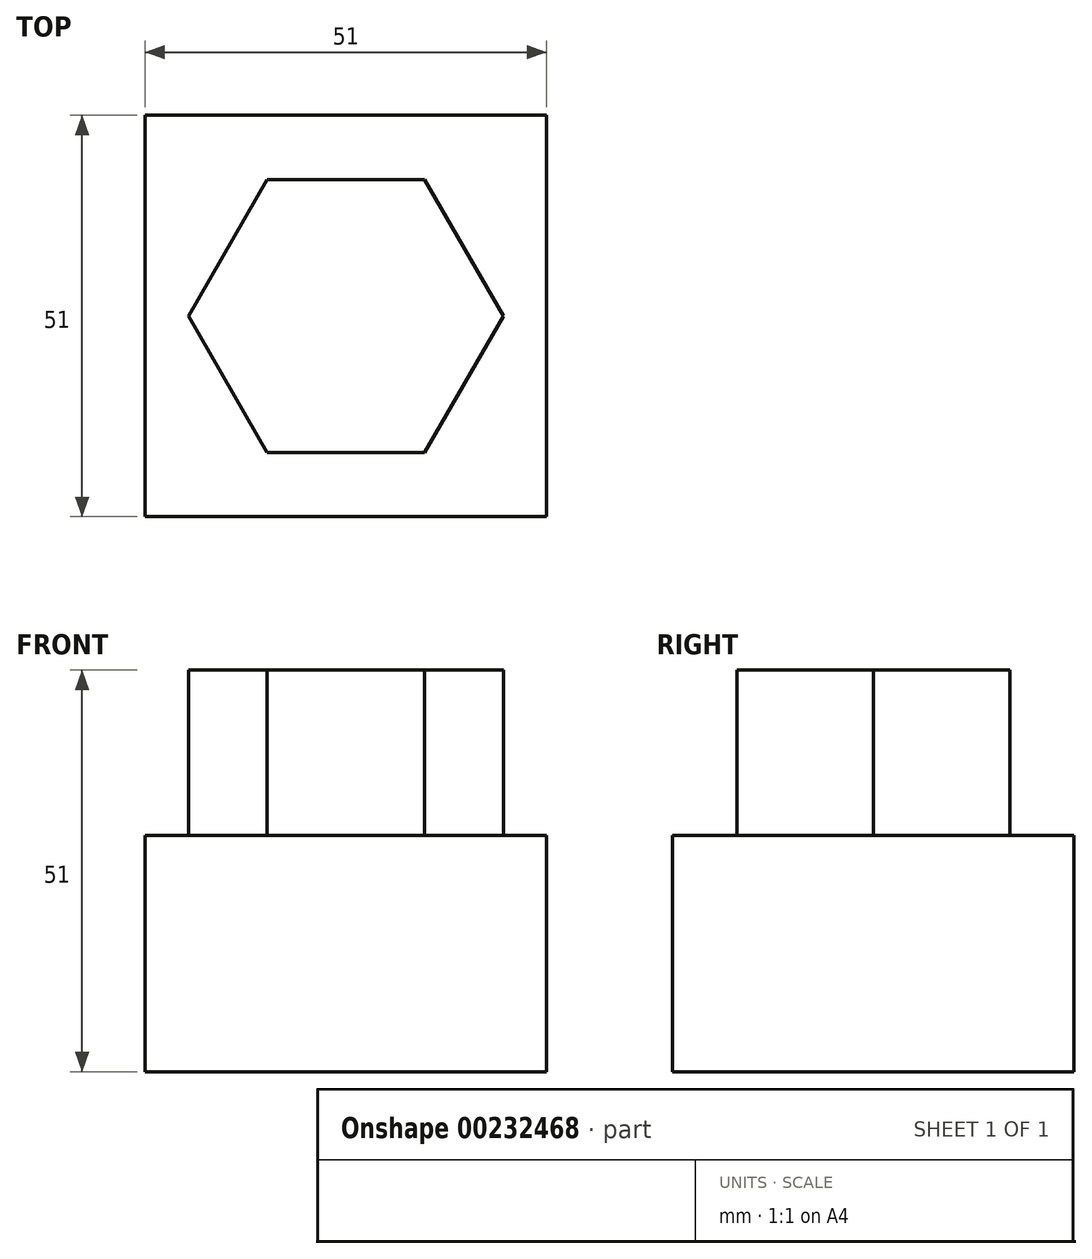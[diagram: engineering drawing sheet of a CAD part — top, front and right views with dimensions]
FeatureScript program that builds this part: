
annotation { "Feature Type Name" : "Feature", "Feature Type Description" : "" }
export const myFeature = defineFeature(function(context is Context, id is Id, definition is map)
    precondition{}
    {
        {
            var Q0;
            Q0=qCreatedBy(makeId("Top.planeOp"),FACE);
            var sketch = newSketch(context, id + "F0", { "sketchPlane" : qUnion([Q0])});
            skLineSegment(sketch, "E0.bottom", {"start": v(-25.5, 25.5) * mm, "end": v(25.5, 25.5) * mm});
            skLineSegment(sketch, "E0.top", {"start": v(-25.5, -25.5) * mm, "end": v(25.5, -25.5) * mm});
            skLineSegment(sketch, "E0.left", {"start": v(-25.5, 25.5) * mm, "end": v(-25.5, -25.5) * mm});
            skLineSegment(sketch, "E0.right", {"start": v(25.5, 25.5) * mm, "end": v(25.5, -25.5) * mm});
            skPoint(sketch, "E0.middle", {"position": v(0, 0) * mm});
            skSolve(sketch);
        }
        {
            var Q0;
            Q0=makeQuery(id+"F0.imprint","IMPRINT",FACE,{"disambiguationData":[TD([[makeQuery(id+"F0.imprint","IMPRINT",EDGE,{"derivedFrom":sQuery(id+"F0.wireOp",EDGE,"E0.bottom")}),-1.0]])]});
            extrude(context, id + "F1", {"entities" : qUnion([Q0]), "depth" : 30 * mm});
        }
        {
            var Q0;
            Q0=makeQuery(id+"F1.opExtrude","CAP_FACE",FACE,{"disambiguationData":[OSD([sQuery(id+"F0.wireOp",EDGE,"E0.bottom"),sQuery(id+"F0.wireOp",EDGE,"E0.top"),sQuery(id+"F0.wireOp",EDGE,"E0.left"),sQuery(id+"F0.wireOp",EDGE,"E0.right")])],"isStart":false});
            var sketch = newSketch(context, id + "F2", { "sketchPlane" : qUnion([Q0])});
            skCircle(sketch, "E1.cCircle", {"center": v(0, 0) * mm, "radius": 20 * mm, "construction": true});
            skLineSegment(sketch, "E1.0", {"start": v(-20, 0) * mm, "end": v(-10, 17.32) * mm});
            skLineSegment(sketch, "E1.1", {"start": v(-10, 17.32) * mm, "end": v(10, 17.32) * mm});
            skLineSegment(sketch, "E1.2", {"start": v(10, 17.32) * mm, "end": v(20, 0) * mm});
            skLineSegment(sketch, "E1.3", {"start": v(20, 0) * mm, "end": v(10, -17.32) * mm});
            skLineSegment(sketch, "E1.4", {"start": v(10, -17.32) * mm, "end": v(-10, -17.32) * mm});
            skLineSegment(sketch, "E1.5", {"start": v(-10, -17.32) * mm, "end": v(-20, 0) * mm});
            skSolve(sketch);
        }
        {
            var Q0;
            Q0=makeQuery(id+"F2.imprint","IMPRINT",FACE,{"disambiguationData":[TD([[makeQuery(id+"F2.imprint","IMPRINT",EDGE,{"derivedFrom":sQuery(id+"F2.wireOp",EDGE,"E1.0")}),-1.0]])]});
            extrude(context, id + "F3", {"entities" : qUnion([Q0]), "operationType" : NewBodyOperationType.ADD, "depth" : 21 * mm});
        }
    });
